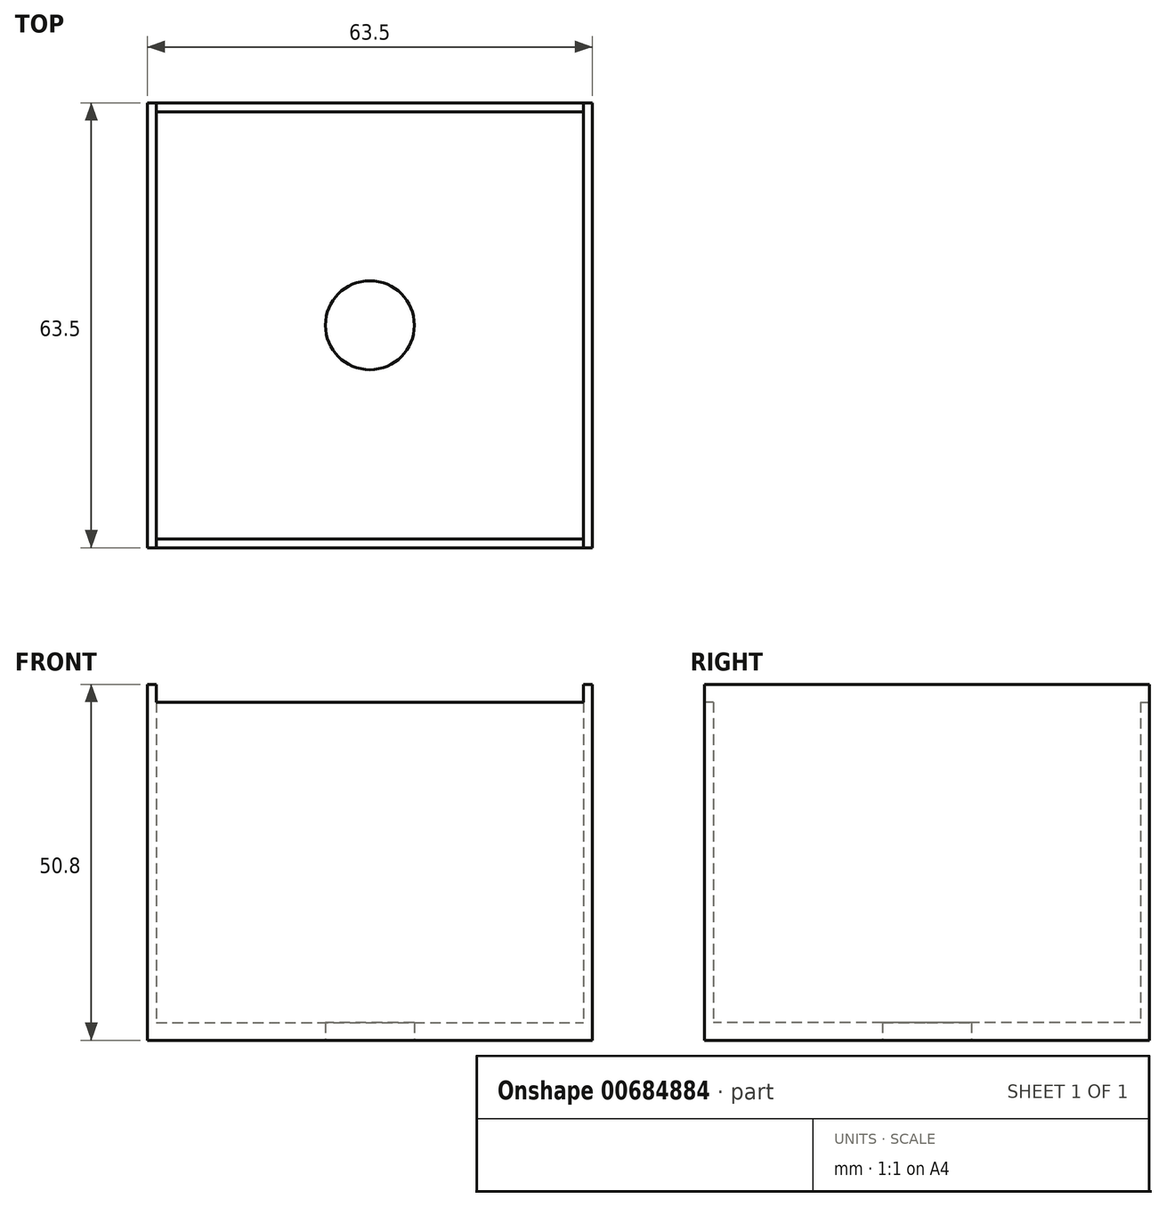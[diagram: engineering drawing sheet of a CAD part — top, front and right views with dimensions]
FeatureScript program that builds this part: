
annotation { "Feature Type Name" : "Feature", "Feature Type Description" : "" }
export const myFeature = defineFeature(function(context is Context, id is Id, definition is map)
    precondition{}
    {
        {
            var Q0;
            Q0=qCreatedBy(makeId("Top.planeOp"),FACE);
            var sketch = newSketch(context, id + "F0", { "sketchPlane" : qUnion([Q0])});
            skLineSegment(sketch, "E0.bottom", {"start": v(-30.48, 30.48) * mm, "end": v(30.48, 30.48) * mm});
            skLineSegment(sketch, "E0.top", {"start": v(-30.48, -30.48) * mm, "end": v(30.48, -30.48) * mm});
            skLineSegment(sketch, "E0.left", {"start": v(-30.48, 30.48) * mm, "end": v(-30.48, -30.48) * mm});
            skLineSegment(sketch, "E0.right", {"start": v(30.48, 30.48) * mm, "end": v(30.48, -30.48) * mm});
            skPoint(sketch, "E0.middle", {"position": v(0, 0) * mm});
            skLineSegment(sketch, "E1.bottom", {"start": v(-31.75, 31.75) * mm, "end": v(31.75, 31.75) * mm});
            skLineSegment(sketch, "E1.top", {"start": v(-31.75, -31.75) * mm, "end": v(31.75, -31.75) * mm});
            skLineSegment(sketch, "E1.left", {"start": v(-31.75, 31.75) * mm, "end": v(-31.75, -31.75) * mm});
            skLineSegment(sketch, "E1.right", {"start": v(31.75, 31.75) * mm, "end": v(31.75, -31.75) * mm});
            skCircle(sketch, "E2", {"center": v(0, 0) * mm, "radius": 6.35 * mm});
            skLineSegment(sketch, "E3", {"start": v(-30.48, -30.48) * mm, "end": v(-30.48, -31.75) * mm});
            skLineSegment(sketch, "E4", {"start": v(-30.48, 30.48) * mm, "end": v(-30.48, 31.75) * mm});
            skLineSegment(sketch, "E5", {"start": v(30.48, 30.48) * mm, "end": v(30.48, 31.75) * mm});
            skLineSegment(sketch, "E6", {"start": v(30.48, -30.48) * mm, "end": v(30.48, -31.75) * mm});
            skSolve(sketch);
        }
        {
            var Q0;
            Q0=makeQuery(id+"F0.imprint","IMPRINT",FACE,{"disambiguationData":[TD([[makeQuery(id+"F0.imprint","IMPRINT",EDGE,{"derivedFrom":sQuery(id+"F0.wireOp",EDGE,"E0.bottom")}),-1.0]])]});
            extrude(context, id + "F1", {"entities" : qUnion([Q0]), "depth" : 2.54 * mm, "offsetDistance" : 25.4 * mm});
        }
        {
            var Q0;
            Q0=makeQuery(id+"F0.imprint","IMPRINT",FACE,{"disambiguationData":[TD([[makeQuery(id+"F0.imprint","IMPRINT",EDGE,{"derivedFrom":sQuery(id+"F0.wireOp",EDGE,"E0.left")}),-1.0]])]});
            var Q1;
            Q1=makeQuery(id+"F0.imprint","IMPRINT",FACE,{"disambiguationData":[TD([[makeQuery(id+"F0.imprint","IMPRINT",EDGE,{"derivedFrom":sQuery(id+"F0.wireOp",EDGE,"E0.right")}),1.0]])]});
            extrude(context, id + "F2", {"entities" : qUnion([Q0, Q1]), "operationType" : NewBodyOperationType.ADD, "depth" : 50.8 * mm, "offsetDistance" : 25.4 * mm});
        }
        {
            var Q0;
            Q0=makeQuery(id+"F0.imprint","IMPRINT",FACE,{"disambiguationData":[TD([[makeQuery(id+"F0.imprint","IMPRINT",EDGE,{"derivedFrom":sQuery(id+"F0.wireOp",EDGE,"E0.top")}),-1.0]])]});
            var Q1;
            Q1=makeQuery(id+"F0.imprint","IMPRINT",FACE,{"disambiguationData":[TD([[makeQuery(id+"F0.imprint","IMPRINT",EDGE,{"derivedFrom":sQuery(id+"F0.wireOp",EDGE,"E0.bottom")}),1.0]])]});
            extrude(context, id + "F3", {"entities" : qUnion([Q0, Q1]), "operationType" : NewBodyOperationType.ADD, "depth" : 48.26 * mm, "offsetDistance" : 25.4 * mm});
        }
    });
